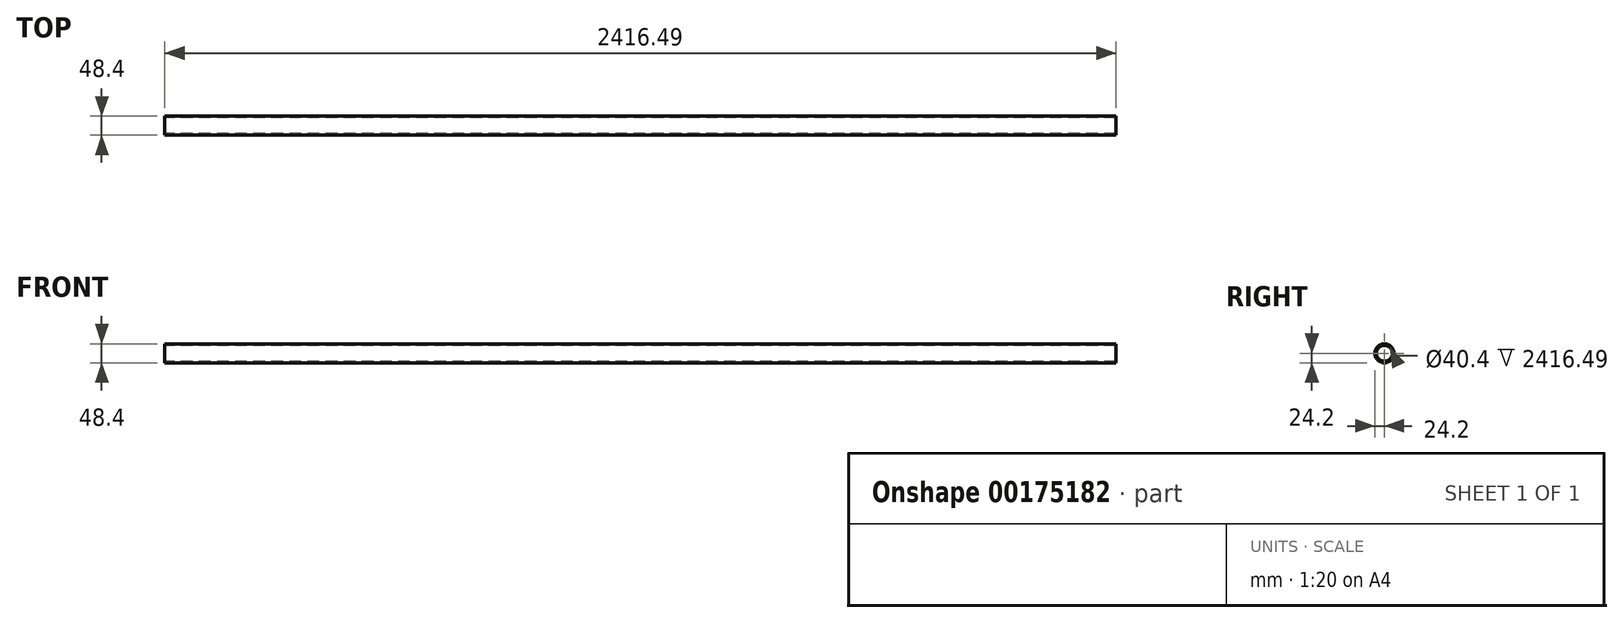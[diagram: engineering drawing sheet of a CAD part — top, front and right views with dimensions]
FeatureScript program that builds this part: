
annotation { "Feature Type Name" : "Feature", "Feature Type Description" : "" }
export const myFeature = defineFeature(function(context is Context, id is Id, definition is map)
    precondition{}
    {
        {
            var Q0;
            Q0=qCreatedBy(makeId("Right.planeOp"),FACE);
            var sketch = newSketch(context, id + "F0", { "sketchPlane" : qUnion([Q0])});
            skCircle(sketch, "E0", {"center": v(0, 0) * mm, "radius": 24.2 * mm});
            skSolve(sketch);
        }
        {
            var Q0;
            Q0 = qSketchRegion(id + "F0", true);
            extrude(context, id + "F1", {"entities" : qUnion([Q0]), "depth" : 2416.49 * mm});
        }
        {
            var Q0;
            Q0=makeQuery(id+"F1.opExtrude","CAP_FACE",FACE,{"disambiguationData":[OSD([sQuery(id+"F0.wireOp",EDGE,"E0")])],"isStart":false});
            var Q1;
            Q1=makeQuery(id+"F1.opExtrude","CAP_FACE",FACE,{"disambiguationData":[OSD([sQuery(id+"F0.wireOp",EDGE,"E0")])],"isStart":true});
            shell(context, id + "F2", {"entities" : qUnion([Q0, Q1]), "thickness" : 4 * mm});
        }
    });
